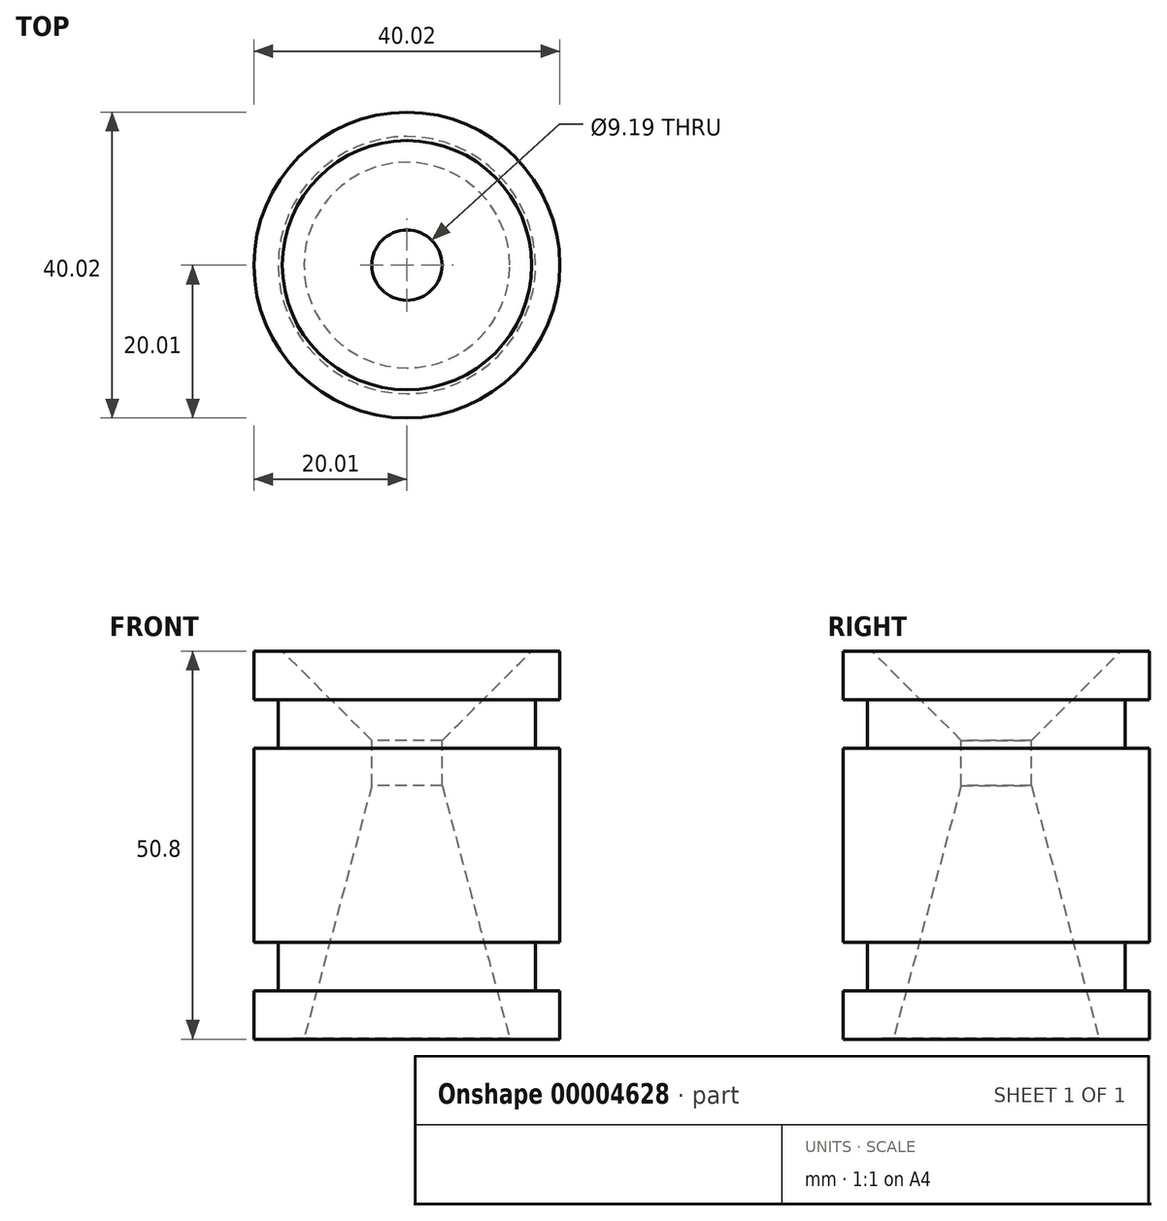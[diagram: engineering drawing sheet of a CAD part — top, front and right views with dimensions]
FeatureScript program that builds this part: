
annotation { "Feature Type Name" : "Feature", "Feature Type Description" : "" }
export const myFeature = defineFeature(function(context is Context, id is Id, definition is map)
    precondition{}
    {
        {
            var Q0;
            Q0=qCreatedBy(makeId("Front.planeOp"),FACE);
            var sketch = newSketch(context, id + "F0", { "sketchPlane" : qUnion([Q0])});
            skLineSegment(sketch, "E0", {"start": v(-20, 50.7) * mm, "end": v(-16.3, 50.7) * mm});
            skPoint(sketch, "E1.orphan", {"position": v(0, 50.7) * mm});
            skLineSegment(sketch, "E2", {"start": v(0, 50.7) * mm, "end": v(0, 0) * mm});
            skLineSegment(sketch, "E3", {"start": v(-20, 44.35) * mm, "end": v(-16.83, 44.35) * mm});
            skLineSegment(sketch, "E4", {"start": v(-16.83, 44.35) * mm, "end": v(-16.83, 38) * mm});
            skLineSegment(sketch, "E5", {"start": v(-16.83, 38) * mm, "end": v(-20, 38) * mm});
            skLineSegment(sketch, "E6", {"start": v(-20, 50.7) * mm, "end": v(-20, 44.35) * mm});
            skLineSegment(sketch, "E7", {"start": v(-20, -0.1) * mm, "end": v(-20, 6.25) * mm});
            skLineSegment(sketch, "E8", {"start": v(-20, 6.25) * mm, "end": v(-16.83, 6.25) * mm});
            skLineSegment(sketch, "E9", {"start": v(-16.83, 6.25) * mm, "end": v(-16.83, 12.6) * mm});
            skLineSegment(sketch, "E10", {"start": v(-16.83, 12.6) * mm, "end": v(-20, 12.6) * mm});
            skLineSegment(sketch, "E11", {"start": v(-20, 38) * mm, "end": v(-20, 12.6) * mm});
            skLineSegment(sketch, "E12", {"start": v(-16.3, 50.7) * mm, "end": v(-4.6, 38.98) * mm});
            skLineSegment(sketch, "E13", {"start": v(-4.6, 38.98) * mm, "end": v(-4.6, 33.08) * mm});
            skLineSegment(sketch, "E14", {"start": v(-4.6, 33.08) * mm, "end": v(-13.46, 0) * mm});
            skLineSegment(sketch, "E15", {"start": v(-20, -0.1) * mm, "end": v(-13.46, 0) * mm});
            skSolve(sketch);
        }
        {
            var Q0;
            Q0=makeQuery(id+"F0.imprint","IMPRINT",FACE,{"disambiguationData":[TD([[makeQuery(id+"F0.imprint","IMPRINT",EDGE,{"derivedFrom":sQuery(id+"F0.wireOp",EDGE,"ae4fbf7d-e562-4bd7-93fc-ba9a87feeb8e")}),-1.0]])]});
            var Q1;
            Q1=makeQuery(id+"F0.imprint","IMPRINT",FACE,{"disambiguationData":[TD([[makeQuery(id+"F0.imprint","IMPRINT",EDGE,{"derivedFrom":sQuery(id+"F0.wireOp",EDGE,"E0")}),-1.0]])]});
            var Q2;
            Q2=sQuery(id+"F0.wireOp",EDGE,"E2");
            revolve(context, id + "F1", {"entities" : qUnion([Q0, Q1]), "axis" : qUnion([Q2]), "revolveType" : RevolveType.FULL});
        }
    });
